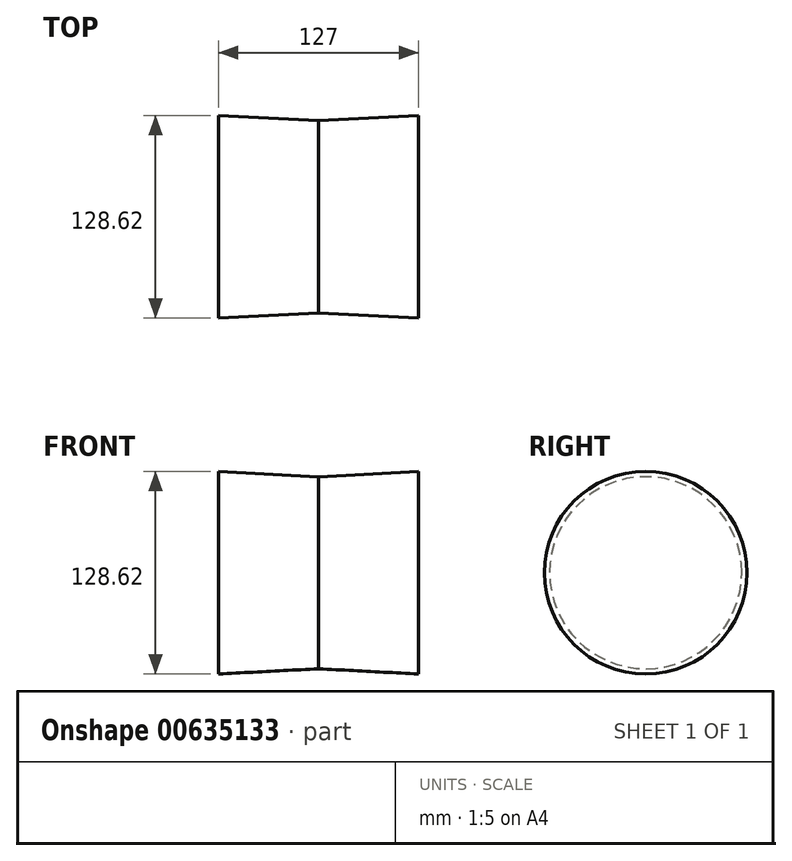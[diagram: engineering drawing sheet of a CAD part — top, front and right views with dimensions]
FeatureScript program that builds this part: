
annotation { "Feature Type Name" : "Feature", "Feature Type Description" : "" }
export const myFeature = defineFeature(function(context is Context, id is Id, definition is map)
    precondition{}
    {
        {
            var Q0;
            Q0=qCreatedBy(makeId("Right.planeOp"),FACE);
            var sketch = newSketch(context, id + "F0", { "sketchPlane" : qUnion([Q0])});
            skCircle(sketch, "E0", {"center": v(0, 0) * mm, "radius": 60.98 * mm});
            skSolve(sketch);
        }
        {
            var Q0;
            Q0=makeQuery(id+"F0.imprint","IMPRINT",FACE,{"disambiguationData":[TD([[makeQuery(id+"F0.imprint","IMPRINT",EDGE,{"derivedFrom":sQuery(id+"F0.wireOp",EDGE,"E0")}),1.0]])]});
            extrude(context, id + "F1", {"entities" : qUnion([Q0]), "endBound" : BoundingType.SYMMETRIC, "depth" : 127 * mm, "offsetDistance" : 25.4 * mm, "hasDraft" : true, "draftAngle" : 3 * degree});
        }
    });
